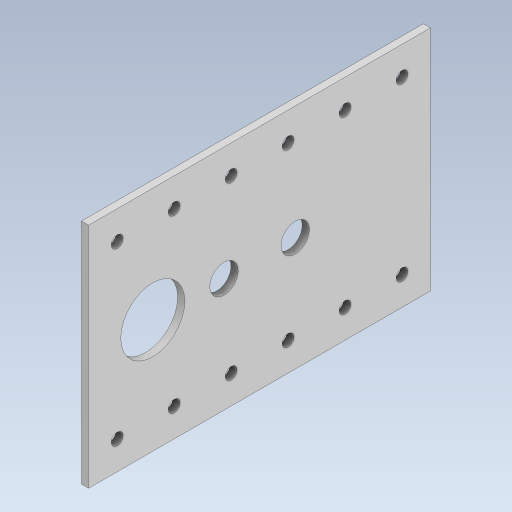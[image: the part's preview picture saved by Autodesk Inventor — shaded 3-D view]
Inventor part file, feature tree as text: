
AUTODESK INVENTOR PART (.ipt)
format: ipt  version: 2023 (Build 270158000, 158)  size: 138,752 bytes
history: native  units: in
note: dims shown in document units (in); Inventor stores cm internally (conversion verified against a paired STEP export)
features: extrude x1, sketch x1
ambient origin geometry x8: Origin, YZ Plane, XZ Plane, XY Plane, X Axis, Y Axis, Z Axis, Center Point
bodies: Solid1 (feature_tree)
feature tree (2):
  extrude  "Extrusion1"  Depth=6.0in
  sketch  "Sketch1"  dims[d0=4.0in d1=6.0in d2=1.125in d3=0.5in d4=0.5in d5=1.125in d6=1.25in d7=1.25in d8=1.25in d9=0.209in d10=0.5in d11=0.5in d12=2.3622in d14=1.0in d15=0.7874in d17=3.0in d20=0.125in d21=0.0in d22=0.5in d23=0.0344in d24=0.5in d25=0.0344in]
